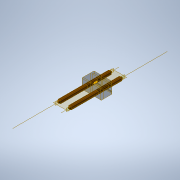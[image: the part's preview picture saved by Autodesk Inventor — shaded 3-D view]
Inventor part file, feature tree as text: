
AUTODESK INVENTOR PART (.ipt)
format: ipt  version: 2020 (Build 240168000, 168)  size: 241,664 bytes
history: native  units: in
note: dims shown in document units (in); Inventor stores cm internally (conversion verified against a paired STEP export)
features: other x8, plane x3
ambient origin geometry x8: Origin, YZ Plane, XZ Plane, XY Plane, X Axis, Y Axis, Z Axis, Center Point
bodies: Solid1 (feature_tree), Solid2 (feature_tree)
feature tree (11):
  other  "Repaired Geometry1"
  plane  "Work Plane1"
  plane  "Work Plane2"
  other  "Work Axis1"
  other  "Work Axis2"
  other  "curve_set_0"
  plane  "Work Plane3"
  other  "brep_1"
  other  "brep_2"
  other  "Composite1"
  other  "Srf1"
